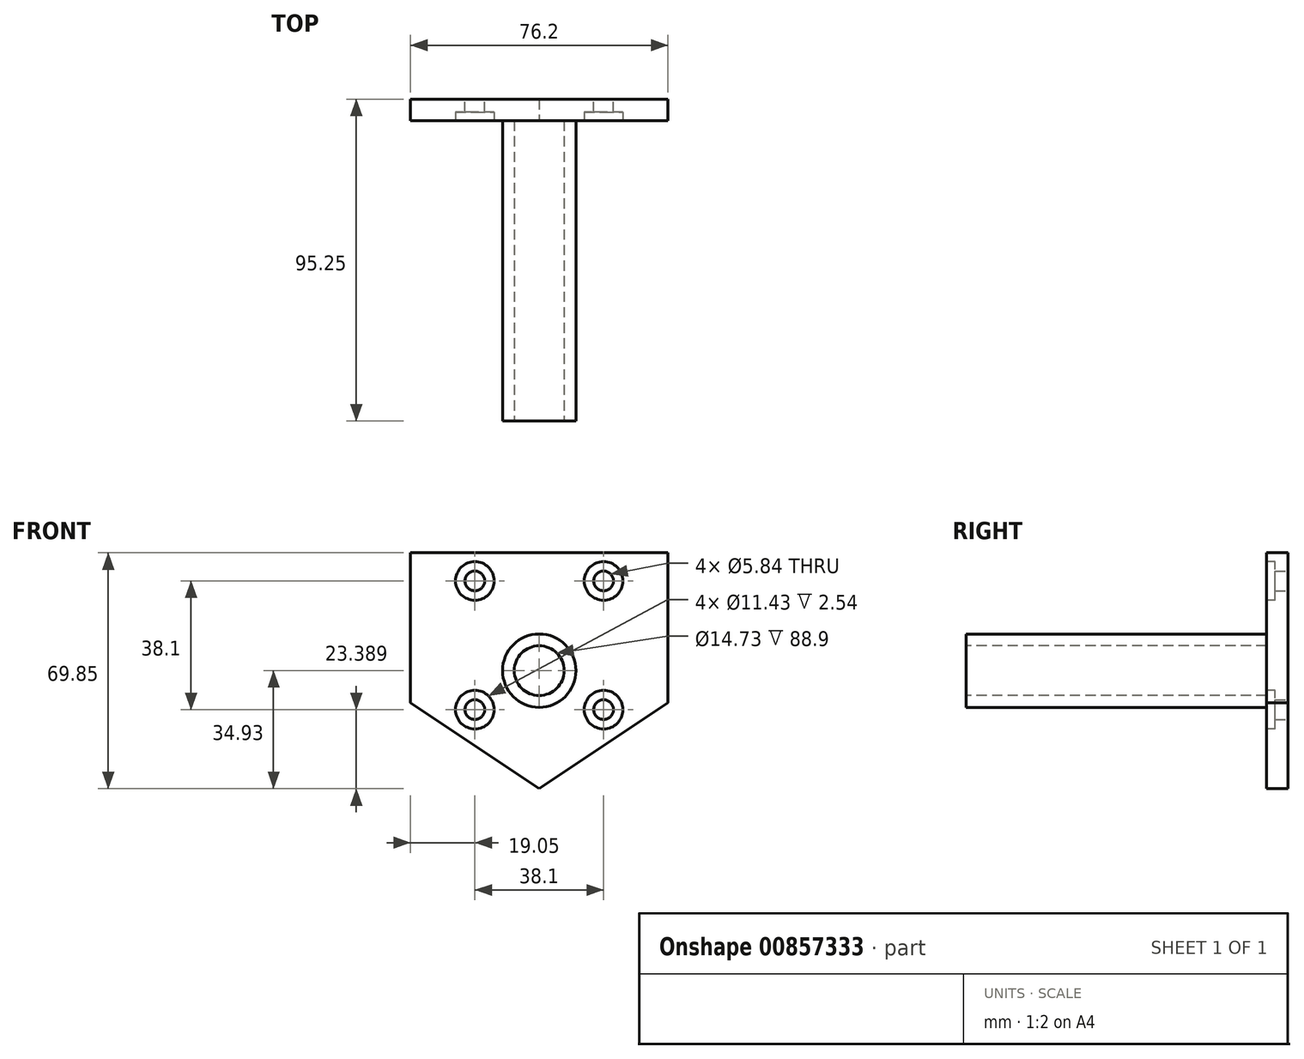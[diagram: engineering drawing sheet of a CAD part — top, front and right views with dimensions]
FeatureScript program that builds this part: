
annotation { "Feature Type Name" : "Feature", "Feature Type Description" : "" }
export const myFeature = defineFeature(function(context is Context, id is Id, definition is map)
    precondition{}
    {
        {
            var Q0;
            Q0=qCreatedBy(makeId("Front.planeOp"),FACE);
            var sketch = newSketch(context, id + "F0", { "sketchPlane" : qUnion([Q0])});
            skCircle(sketch, "E0", {"center": v(0, 0) * mm, "radius": 10.85 * mm});
            skSolve(sketch);
        }
        {
            var Q0;
            Q0 = qSketchRegion(id + "F0", true);
            extrude(context, id + "F1", {"entities" : qUnion([Q0]), "depth" : 88.9 * mm, "offsetDistance" : 25.4 * mm});
        }
        {
            var Q0;
            Q0=makeQuery(id+"F1.opExtrude","CAP_FACE",FACE,{"disambiguationData":[OSD([sQuery(id+"F0.wireOp",EDGE,"E0")])],"isStart":false});
            var sketch = newSketch(context, id + "F2", { "sketchPlane" : qUnion([Q0])});
            skPoint(sketch, "E1", {"position": v(0, 0) * mm});
            skSolve(sketch);
        }
        {
            var Q0;
            Q0=sQuery(id+"F2.wireOp",VERTEX,"E1");
            var Q1;
            Q1=makeQuery(id+"F1.opExtrude","SWEPT_BODY",BODY,{"disambiguationData":[OSD([sQuery(id+"F0.wireOp",EDGE,"E0")])]});
            hole(context, id + "F3", {"style" : HoleStyle.SIMPLE, "endStyle" : HoleEndStyle.THROUGH, "holeDiameter" : 14.73 * mm, "majorDiameter" : 6.35 * mm, "tappedDepth" : 12.7 * mm, "tapClearance" : 3, "locations" : qUnion([Q0]), "scope" : qUnion([Q1])});
        }
        {
            var Q0;
            Q0=qCreatedBy(makeId("Front.planeOp"),FACE);
            var sketch = newSketch(context, id + "F4", { "sketchPlane" : qUnion([Q0])});
            skLineSegment(sketch, "E2", {"start": v(0, 34.93) * mm, "end": v(-38.1, 34.92) * mm});
            skLineSegment(sketch, "E3", {"start": v(0, 34.93) * mm, "end": v(38.1, 34.93) * mm});
            skLineSegment(sketch, "E4", {"start": v(-38.1, 34.92) * mm, "end": v(-38.1, -9.53) * mm});
            skLineSegment(sketch, "E5", {"start": v(0, 0) * mm, "end": v(0, 34.93) * mm});
            skLineSegment(sketch, "E6", {"start": v(0, 0) * mm, "end": v(0, -34.93) * mm});
            skLineSegment(sketch, "E7", {"start": v(38.1, 34.93) * mm, "end": v(38.1, -9.52) * mm});
            skLineSegment(sketch, "E8", {"start": v(-38.1, -9.52) * mm, "end": v(0, -34.93) * mm});
            skLineSegment(sketch, "E9", {"start": v(38.1, -9.52) * mm, "end": v(0, -34.93) * mm});
            skSolve(sketch);
        }
        {
            var Q0;
            Q0 = qSketchRegion(id + "F4", true);
            extrude(context, id + "F5", {"entities" : qUnion([Q0]), "operationType" : NewBodyOperationType.ADD, "oppositeDirection" : true, "depth" : 6.35 * mm, "offsetDistance" : 25.4 * mm});
        }
        {
            var Q0;
            Q0=makeQuery(id+"F5.opExtrude","CAP_FACE",FACE,{"disambiguationData":[OSD([sQuery(id+"F4.wireOp",EDGE,"E2"),sQuery(id+"F4.wireOp",EDGE,"E3"),sQuery(id+"F4.wireOp",EDGE,"E4"),sQuery(id+"F4.wireOp",EDGE,"E7"),sQuery(id+"F4.wireOp",EDGE,"E8"),sQuery(id+"F4.wireOp",EDGE,"E9")])],"isStart":false});
            var sketch = newSketch(context, id + "F6", { "sketchPlane" : qUnion([Q0])});
            skPoint(sketch, "E10", {"position": v(-19.05, -11.54) * mm});
            skPoint(sketch, "E11", {"position": v(19.05, -11.54) * mm});
            skPoint(sketch, "E12", {"position": v(-19.05, 26.56) * mm});
            skPoint(sketch, "E13", {"position": v(19.05, 26.56) * mm});
            skSolve(sketch);
        }
        {
            var Q0;
            Q0=sQuery(id+"F6.wireOp",VERTEX,"E12");
            var Q1;
            Q1=sQuery(id+"F6.wireOp",VERTEX,"E13");
            var Q2;
            Q2=sQuery(id+"F6.wireOp",VERTEX,"E11");
            var Q3;
            Q3=sQuery(id+"F6.wireOp",VERTEX,"E10");
            var Q4;
            Q4=makeQuery(id+"F1.opExtrude","SWEPT_BODY",BODY,{"disambiguationData":[OSD([sQuery(id+"F0.wireOp",EDGE,"E0")])]});
            hole(context, id + "F7", {"style" : HoleStyle.SIMPLE, "endStyle" : HoleEndStyle.THROUGH, "holeDiameter" : 5.84 * mm, "majorDiameter" : 6.35 * mm, "tappedDepth" : 12.7 * mm, "tapClearance" : 3, "locations" : qUnion([Q0, Q1, Q2, Q3]), "scope" : qUnion([Q4])});
        }
        {
            var Q0;
            {var subQ0=sQuery(id+"F4.wireOp",EDGE,"E7");var subQ1=sQuery(id+"F4.wireOp",EDGE,"E4");var subQ2=sQuery(id+"F4.wireOp",EDGE,"E3");var subQ3=sQuery(id+"F4.wireOp",EDGE,"E2");var subQ4=sQuery(id+"F4.wireOp",EDGE,"E8");var subQ5=sQuery(id+"F4.wireOp",EDGE,"E9");Q0=makeQuery(id+"F5.boolean.opBoolean","SPLIT",FACE,{"disambiguationData":[TD([makeQuery(id+"F1.opExtrude","SWEPT_FACE",FACE,{"disambiguationData":[OSD([sQuery(id+"F0.wireOp",EDGE,"E0")])]})])],"derivedFrom":makeQuery(id+"F5.opExtrude","CAP_FACE",FACE,{"disambiguationData":[OSD([subQ3,subQ2,subQ1,subQ0,subQ4,subQ5])],"isStart":true})});}
            var sketch = newSketch(context, id + "F8", { "sketchPlane" : qUnion([Q0])});
            skCircle(sketch, "E14", {"center": v(-19.05, 26.56) * mm, "radius": 5.72 * mm});
            skCircle(sketch, "E15", {"center": v(19.05, 26.56) * mm, "radius": 5.72 * mm});
            skCircle(sketch, "E16", {"center": v(-19.05, -11.54) * mm, "radius": 5.72 * mm});
            skCircle(sketch, "E17", {"center": v(19.05, -11.54) * mm, "radius": 5.72 * mm});
            skSolve(sketch);
        }
        {
            var Q0;
            Q0 = qSketchRegion(id + "F8", true);
            extrude(context, id + "F9", {"entities" : qUnion([Q0]), "operationType" : NewBodyOperationType.REMOVE, "oppositeDirection" : true, "depth" : 2.54 * mm, "offsetDistance" : 25.4 * mm});
        }
    });
